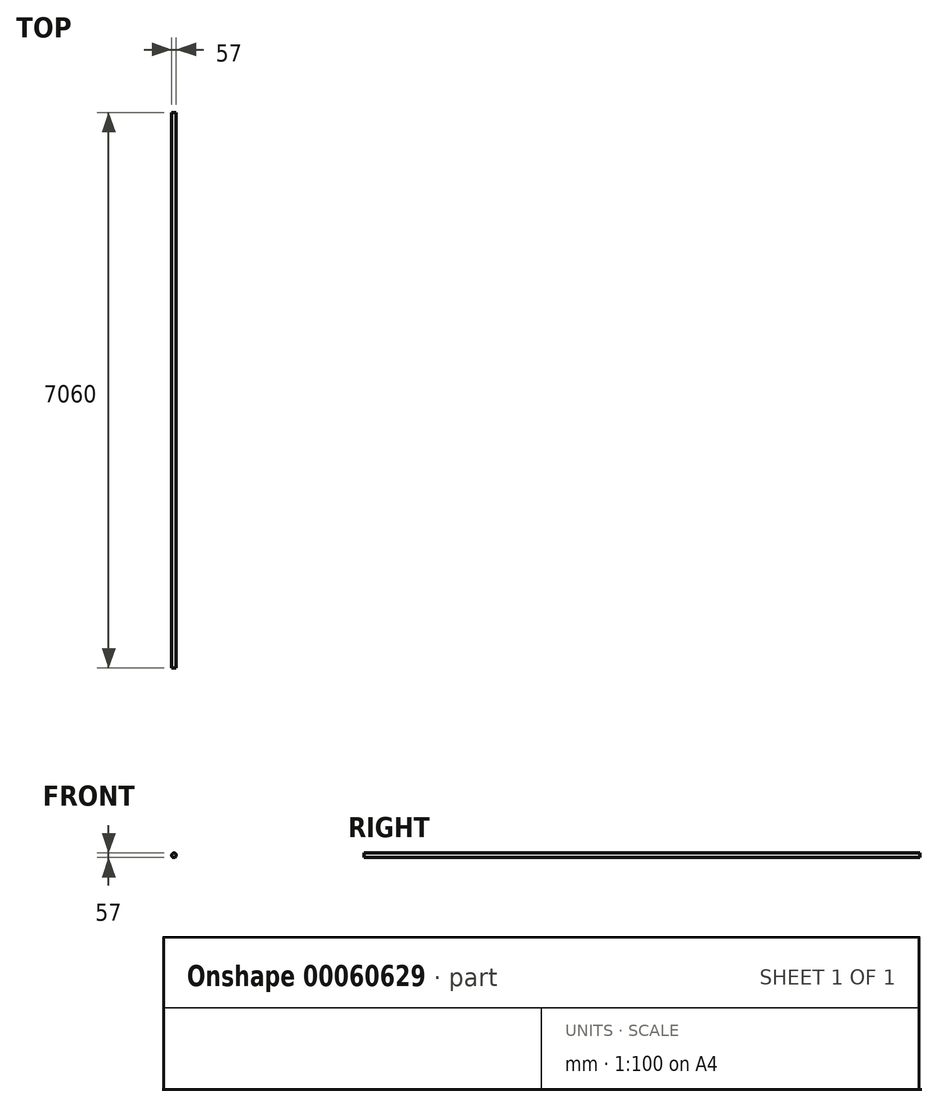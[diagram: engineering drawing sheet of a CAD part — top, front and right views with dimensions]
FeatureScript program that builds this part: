
annotation { "Feature Type Name" : "Feature", "Feature Type Description" : "" }
export const myFeature = defineFeature(function(context is Context, id is Id, definition is map)
    precondition{}
    {
        {
            var Q0;
            Q0=qCreatedBy(makeId("Front.planeOp"),FACE);
            var sketch = newSketch(context, id + "F0", { "sketchPlane" : qUnion([Q0])});
            skCircle(sketch, "E0", {"center": v(0, 0) * mm, "radius": 28.5 * mm});
            skSolve(sketch);
        }
        {
            var Q0;
            Q0=makeQuery(id+"F0.imprint","IMPRINT",FACE,{"disambiguationData":[TD([[makeQuery(id+"F0.imprint","IMPRINT",EDGE,{"derivedFrom":sQuery(id+"F0.wireOp",EDGE,"E0")}),1.0]])]});
            extrude(context, id + "F1", {"entities" : qUnion([Q0]), "depth" : 7060 * mm});
        }
    });
